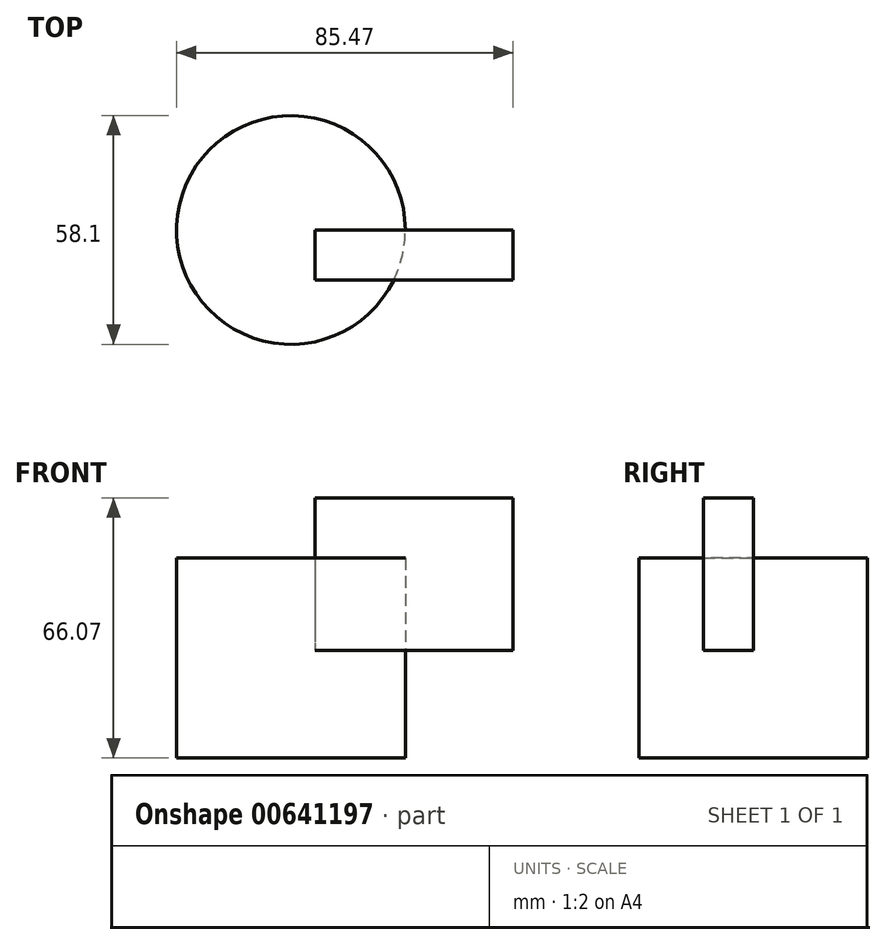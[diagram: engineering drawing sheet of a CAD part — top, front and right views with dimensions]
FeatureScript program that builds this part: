
annotation { "Feature Type Name" : "Feature", "Feature Type Description" : "" }
export const myFeature = defineFeature(function(context is Context, id is Id, definition is map)
    precondition{}
    {
        {
            var Q0;
            Q0=qCreatedBy(makeId("Top.planeOp"),FACE);
            var sketch = newSketch(context, id + "F0", { "sketchPlane" : qUnion([Q0])});
            skCircle(sketch, "E0", {"center": v(0, 0) * mm, "radius": 29.05 * mm});
            skSolve(sketch);
        }
        {
            var Q0;
            Q0=makeQuery(id+"F0.imprint","IMPRINT",FACE,{"disambiguationData":[TD([[makeQuery(id+"F0.imprint","IMPRINT",EDGE,{"derivedFrom":sQuery(id+"F0.wireOp",EDGE,"E0")}),1.0]])]});
            extrude(context, id + "F1", {"entities" : qUnion([Q0]), "depth" : 50.8 * mm, "offsetDistance" : 25.4 * mm});
        }
        {
            var Q0;
            Q0=qCreatedBy(makeId("Front.planeOp"),FACE);
            var sketch = newSketch(context, id + "F2", { "sketchPlane" : qUnion([Q0])});
            skLineSegment(sketch, "E1.bottom", {"start": v(6.1, 66.07) * mm, "end": v(56.42, 66.07) * mm});
            skLineSegment(sketch, "E1.top", {"start": v(6.1, 27.27) * mm, "end": v(56.42, 27.27) * mm});
            skLineSegment(sketch, "E1.left", {"start": v(6.1, 66.07) * mm, "end": v(6.1, 27.27) * mm});
            skLineSegment(sketch, "E1.right", {"start": v(56.42, 66.07) * mm, "end": v(56.42, 27.27) * mm});
            skSolve(sketch);
        }
        {
            var Q0;
            Q0=makeQuery(id+"F2.imprint","IMPRINT",FACE,{"disambiguationData":[TD([[makeQuery(id+"F2.imprint","IMPRINT",EDGE,{"derivedFrom":sQuery(id+"F2.wireOp",EDGE,"E1.bottom")}),-1.0]])]});
            extrude(context, id + "F3", {"entities" : qUnion([Q0]), "depth" : 12.7 * mm, "offsetDistance" : 25.4 * mm});
        }
    });
